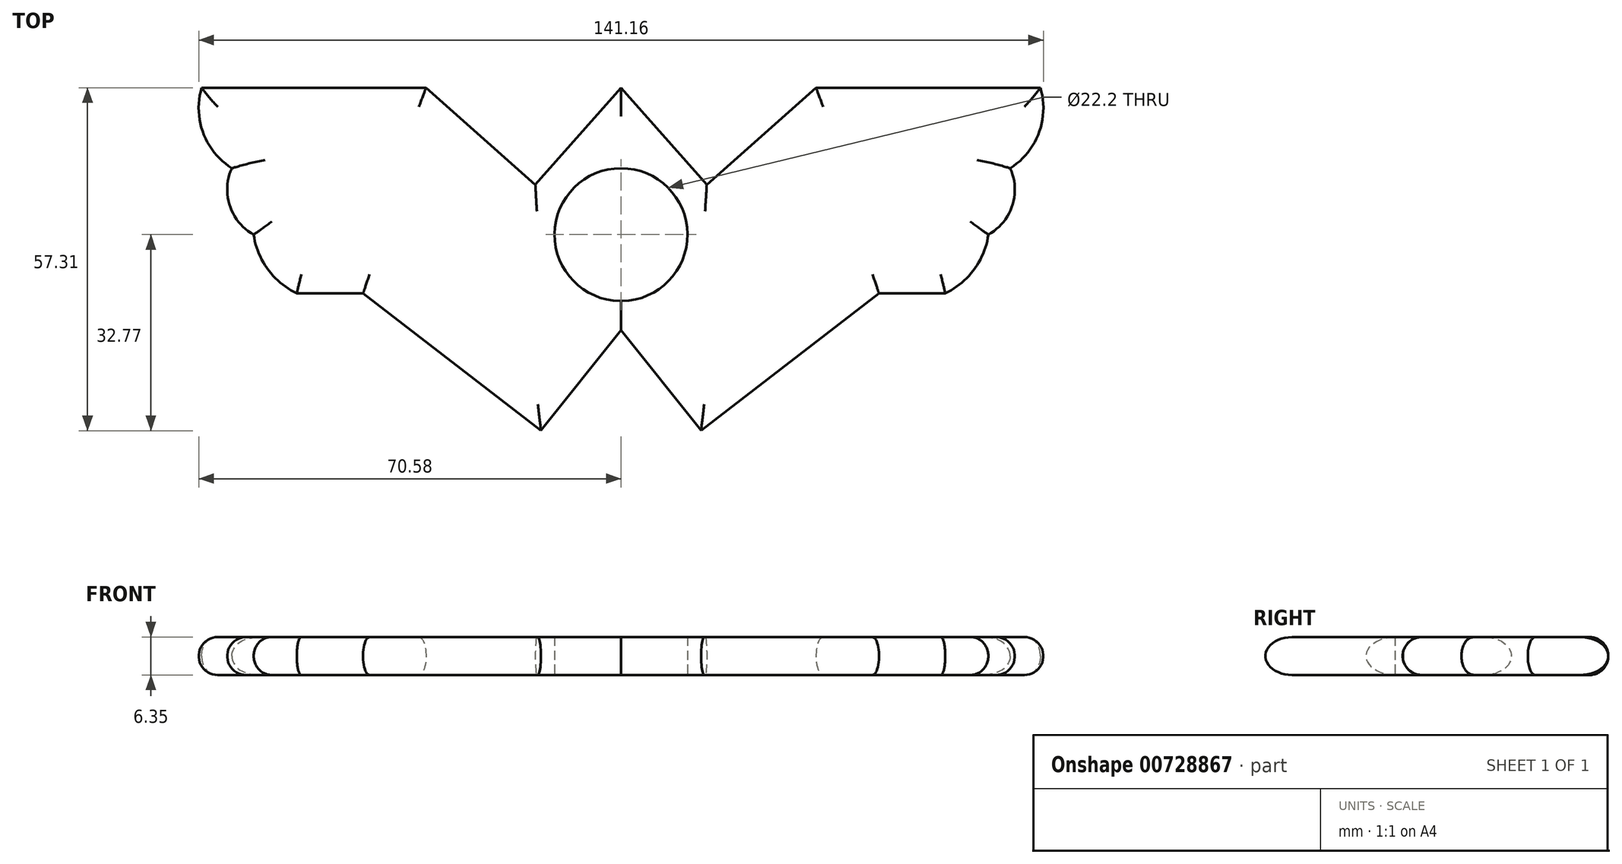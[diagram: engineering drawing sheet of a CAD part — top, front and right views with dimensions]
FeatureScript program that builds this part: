
annotation { "Feature Type Name" : "Feature", "Feature Type Description" : "" }
export const myFeature = defineFeature(function(context is Context, id is Id, definition is map)
    precondition{}
    {
        {
            var Q0;
            Q0=qCreatedBy(makeId("Top.planeOp"),FACE);
            var sketch = newSketch(context, id + "F0", { "sketchPlane" : qUnion([Q0])});
            skLineSegment(sketch, "E0", {"start": v(0, 24.54) * mm, "end": v(-14.33, 8.37) * mm});
            skLineSegment(sketch, "E1", {"start": v(-14.33, 8.37) * mm, "end": v(-32.58, 24.54) * mm});
            skLineSegment(sketch, "E2", {"start": v(-32.58, 24.54) * mm, "end": v(-56.32, 24.54) * mm});
            skLineSegment(sketch, "E3.MirrorCS", {"start": v(0, 24.54) * mm, "end": v(14.33, 8.37) * mm});
            skLineSegment(sketch, "E4.MirrorCS", {"start": v(32.58, 24.54) * mm, "end": v(56.32, 24.54) * mm});
            skLineSegment(sketch, "E5.MirrorCS", {"start": v(14.33, 8.37) * mm, "end": v(32.58, 24.54) * mm});
            skLineSegment(sketch, "E6.1.0.1", {"start": v(-14.14, -13.63) * mm, "end": v(-18.37, -9.88) * mm});
            skLineSegment(sketch, "E6.1.0.3", {"start": v(8.6, -6.95) * mm, "end": v(14.51, -13.63) * mm});
            skLineSegment(sketch, "E6.1.0.4", {"start": v(14.51, -13.63) * mm, "end": v(18.55, -10.06) * mm});
            skPoint(sketch, "E7.orphan", {"position": v(32.77, 2.54) * mm});
            skLineSegment(sketch, "E8", {"start": v(39.4, 8.41) * mm, "end": v(42.4, 11.07) * mm});
            skLineSegment(sketch, "E9", {"start": v(42.4, 11.07) * mm, "end": v(51.59, 11.08) * mm});
            skLineSegment(sketch, "E10", {"start": v(42.21, 0) * mm, "end": v(51.59, 0) * mm});
            skLineSegment(sketch, "E11", {"start": v(51.59, 11.08) * mm, "end": v(51.59, 11.08) * mm});
            skLineSegment(sketch, "E12", {"start": v(56.32, 24.54) * mm, "end": v(70.09, 24.54) * mm});
            skLineSegment(sketch, "E13", {"start": v(51.59, 11.08) * mm, "end": v(65.04, 11.1) * mm});
            skArc(sketch, "E14", {"start": v(65.04, 11.1) * mm, "mid": v(69.82, 16.97) * mm, "end": v(70.09, 24.54) * mm});
            skArc(sketch, "E15", {"start": v(61.4, 0) * mm, "mid": v(65.39, 4.84) * mm, "end": v(65.04, 11.1) * mm});
            skLineSegment(sketch, "E16.MirrorCS", {"start": v(-39.4, 8.41) * mm, "end": v(-42.4, 11.07) * mm});
            skLineSegment(sketch, "E17.MirrorCS", {"start": v(-42.4, 11.07) * mm, "end": v(-51.59, 11.08) * mm});
            skLineSegment(sketch, "E18.MirrorCS", {"start": v(-51.59, 11.08) * mm, "end": v(-51.59, 11.08) * mm});
            skLineSegment(sketch, "E19.MirrorCS", {"start": v(-51.59, 11.08) * mm, "end": v(-65.04, 11.1) * mm});
            skLineSegment(sketch, "E20.MirrorCS", {"start": v(-56.32, 24.54) * mm, "end": v(-70.09, 24.54) * mm});
            skArc(sketch, "E21.MirrorCS", {"start": v(-65.04, 11.1) * mm, "mid": v(-69.82, 16.97) * mm, "end": v(-70.09, 24.54) * mm});
            skArc(sketch, "E22.MirrorCS", {"start": v(-61.4, 0) * mm, "mid": v(-65.39, 4.84) * mm, "end": v(-65.04, 11.1) * mm});
            skLineSegment(sketch, "E23.1.0.0", {"start": v(0, -15.96) * mm, "end": v(-13.37, -32.77) * mm});
            skLineSegment(sketch, "E23.1.0.3", {"start": v(-43.11, -9.81) * mm, "end": v(-54.19, -9.81) * mm});
            skLineSegment(sketch, "E23.1.0.4", {"start": v(-52.8, -9.4) * mm, "end": v(-54.19, -9.81) * mm});
            skLineSegment(sketch, "E24", {"start": v(51.59, 0) * mm, "end": v(61.4, 0) * mm});
            skLineSegment(sketch, "E25.MirrorCS", {"start": v(-51.59, 0) * mm, "end": v(-61.4, 0) * mm});
            skLineSegment(sketch, "E26.MirrorCS", {"start": v(-42.21, 0) * mm, "end": v(-51.59, 0) * mm});
            skArc(sketch, "E27.MirrorCS", {"start": v(-54.19, -9.81) * mm, "mid": v(-59.02, -5.8) * mm, "end": v(-61.4, 0) * mm});
            skPoint(sketch, "E28.orphan", {"position": v(58.34, -6.26) * mm});
            skPoint(sketch, "E29.orphan", {"position": v(-65.12, -13.12) * mm});
            skLineSegment(sketch, "E30.trimOffspring", {"start": v(-8.41, -7.16) * mm, "end": v(-14.14, -13.63) * mm});
            skPoint(sketch, "E31.orphan", {"position": v(0.19, 2.54) * mm});
            skPoint(sketch, "E32.orphan", {"position": v(-32.77, 2.54) * mm});
            skPoint(sketch, "E33.orphan", {"position": v(-32.4, 2.54) * mm});
            skLineSegment(sketch, "E34.trimOffspring", {"start": v(-56.16, 0) * mm, "end": v(-56.13, 2.54) * mm, "construction": true});
            skLineSegment(sketch, "E35", {"start": v(-61.4, 0) * mm, "end": v(-42.21, 0) * mm});
            skLineSegment(sketch, "E36", {"start": v(42.21, 0) * mm, "end": v(61.4, 0) * mm});
            skPoint(sketch, "E23.1.0.7.end.orphan", {"position": v(59.36, -13.37) * mm});
            skPoint(sketch, "E23.1.0.8.start.orphan", {"position": v(50.04, -13.37) * mm});
            skPoint(sketch, "E37.start.orphan", {"position": v(54.19, -9.81) * mm});
            skLineSegment(sketch, "E38.MirrorCS", {"start": v(0, -15.96) * mm, "end": v(13.37, -32.77) * mm});
            skLineSegment(sketch, "E39.MirrorCS", {"start": v(43.11, -9.81) * mm, "end": v(54.19, -9.81) * mm});
            skArc(sketch, "E40.MirrorCS", {"start": v(54.19, -9.81) * mm, "mid": v(59.02, -5.8) * mm, "end": v(61.4, 0) * mm});
            skPoint(sketch, "E23.1.0.2.start.orphan", {"position": v(-27.1, -21.7) * mm});
            skPoint(sketch, "E23.1.0.1.end.orphan", {"position": v(-27.42, -21.7) * mm});
            skPoint(sketch, "E41.MirrorCS.end.orphan", {"position": v(27.42, -21.7) * mm});
            skPoint(sketch, "E41.MirrorCS.start.orphan", {"position": v(13.37, -32.77) * mm});
            skPoint(sketch, "E42.MirrorCS.end.orphan", {"position": v(43.11, -9.81) * mm});
            skPoint(sketch, "E42.MirrorCS.start.orphan", {"position": v(27.1, -21.7) * mm});
            skLineSegment(sketch, "E43", {"start": v(-43.11, -9.81) * mm, "end": v(-13.37, -32.77) * mm});
            skLineSegment(sketch, "E44.MirrorCS", {"start": v(43.11, -9.81) * mm, "end": v(13.37, -32.77) * mm});
            skCircle(sketch, "E45", {"center": v(0, 0) * mm, "radius": 11.1 * mm});
            skLineSegment(sketch, "E46", {"start": v(-39.4, 8.41) * mm, "end": v(-18.37, -9.88) * mm});
            skLineSegment(sketch, "E47", {"start": v(39.4, 8.41) * mm, "end": v(18.55, -10.06) * mm});
            skSolve(sketch);
        }
        {
            var Q0;
            Q0=qSketchRegion(id+"F0",true);
            extrude(context, id + "F1", {"entities" : qUnion([Q0]), "depth" : 6.35 * mm, "offsetDistance" : 25.4 * mm});
        }
        {
            var Q0;
            Q0=makeQuery(id+"F1.opExtrude","CAP_EDGE",EDGE,{"disambiguationData":[OSD([sQuery(id+"F0.wireOp",EDGE,"E2"),sQuery(id+"F0.wireOp",EDGE,"E20.MirrorCS")])],"isStart":false});
            var Q1;
            Q1=makeQuery(id+"F1.opExtrude","CAP_EDGE",EDGE,{"disambiguationData":[OSD([sQuery(id+"F0.wireOp",EDGE,"E22.MirrorCS")])],"isStart":false});
            var Q2;
            Q2=makeQuery(id+"F1.opExtrude","CAP_EDGE",EDGE,{"disambiguationData":[OSD([sQuery(id+"F0.wireOp",EDGE,"E27.MirrorCS")])],"isStart":false});
            var Q3;
            Q3=makeQuery(id+"F1.opExtrude","CAP_EDGE",EDGE,{"disambiguationData":[OSD([sQuery(id+"F0.wireOp",EDGE,"E23.1.0.3")])],"isStart":false});
            var Q4;
            Q4=makeQuery(id+"F1.opExtrude","CAP_EDGE",EDGE,{"disambiguationData":[OSD([sQuery(id+"F0.wireOp",EDGE,"E43")])],"isStart":false});
            var Q5;
            Q5=makeQuery(id+"F1.opExtrude","CAP_EDGE",EDGE,{"disambiguationData":[OSD([sQuery(id+"F0.wireOp",EDGE,"E23.1.0.0")])],"isStart":false});
            var Q6;
            Q6=makeQuery(id+"F1.opExtrude","CAP_EDGE",EDGE,{"disambiguationData":[OSD([sQuery(id+"F0.wireOp",EDGE,"E38.MirrorCS")])],"isStart":false});
            var Q7;
            Q7=makeQuery(id+"F1.opExtrude","CAP_EDGE",EDGE,{"disambiguationData":[OSD([sQuery(id+"F0.wireOp",EDGE,"E44.MirrorCS")])],"isStart":false});
            var Q8;
            Q8=makeQuery(id+"F1.opExtrude","CAP_EDGE",EDGE,{"disambiguationData":[OSD([sQuery(id+"F0.wireOp",EDGE,"E39.MirrorCS")])],"isStart":false});
            var Q9;
            Q9=makeQuery(id+"F1.opExtrude","CAP_EDGE",EDGE,{"disambiguationData":[OSD([sQuery(id+"F0.wireOp",EDGE,"E40.MirrorCS")])],"isStart":false});
            var Q10;
            Q10=makeQuery(id+"F1.opExtrude","CAP_EDGE",EDGE,{"disambiguationData":[OSD([sQuery(id+"F0.wireOp",EDGE,"E1")])],"isStart":false});
            var Q11;
            Q11=makeQuery(id+"F1.opExtrude","CAP_EDGE",EDGE,{"disambiguationData":[OSD([sQuery(id+"F0.wireOp",EDGE,"E0")])],"isStart":false});
            var Q12;
            Q12=makeQuery(id+"F1.opExtrude","CAP_EDGE",EDGE,{"disambiguationData":[OSD([sQuery(id+"F0.wireOp",EDGE,"E3.MirrorCS")])],"isStart":false});
            var Q13;
            Q13=makeQuery(id+"F1.opExtrude","CAP_EDGE",EDGE,{"disambiguationData":[OSD([sQuery(id+"F0.wireOp",EDGE,"E5.MirrorCS")])],"isStart":false});
            var Q14;
            Q14=makeQuery(id+"F1.opExtrude","CAP_EDGE",EDGE,{"disambiguationData":[OSD([sQuery(id+"F0.wireOp",EDGE,"E4.MirrorCS"),sQuery(id+"F0.wireOp",EDGE,"E12")])],"isStart":false});
            var Q15;
            Q15=makeQuery(id+"F1.opExtrude","CAP_EDGE",EDGE,{"disambiguationData":[OSD([sQuery(id+"F0.wireOp",EDGE,"E14")])],"isStart":false});
            var Q16;
            Q16=makeQuery(id+"F1.opExtrude","CAP_EDGE",EDGE,{"disambiguationData":[OSD([sQuery(id+"F0.wireOp",EDGE,"E4.MirrorCS"),sQuery(id+"F0.wireOp",EDGE,"E12")])],"isStart":true});
            var Q17;
            Q17=makeQuery(id+"F1.opExtrude","CAP_EDGE",EDGE,{"disambiguationData":[OSD([sQuery(id+"F0.wireOp",EDGE,"E5.MirrorCS")])],"isStart":true});
            var Q18;
            Q18=makeQuery(id+"F1.opExtrude","CAP_EDGE",EDGE,{"disambiguationData":[OSD([sQuery(id+"F0.wireOp",EDGE,"E21.MirrorCS")])],"isStart":true});
            var Q19;
            Q19=makeQuery(id+"F1.opExtrude","CAP_EDGE",EDGE,{"disambiguationData":[OSD([sQuery(id+"F0.wireOp",EDGE,"E27.MirrorCS")])],"isStart":true});
            var Q20;
            Q20=makeQuery(id+"F1.opExtrude","CAP_EDGE",EDGE,{"disambiguationData":[OSD([sQuery(id+"F0.wireOp",EDGE,"E23.1.0.3")])],"isStart":true});
            var Q21;
            Q21=makeQuery(id+"F1.opExtrude","CAP_EDGE",EDGE,{"disambiguationData":[OSD([sQuery(id+"F0.wireOp",EDGE,"E43")])],"isStart":true});
            var Q22;
            Q22=makeQuery(id+"F1.opExtrude","CAP_EDGE",EDGE,{"disambiguationData":[OSD([sQuery(id+"F0.wireOp",EDGE,"E23.1.0.0")])],"isStart":true});
            var Q23;
            Q23=makeQuery(id+"F1.opExtrude","CAP_EDGE",EDGE,{"disambiguationData":[OSD([sQuery(id+"F0.wireOp",EDGE,"E38.MirrorCS")])],"isStart":true});
            var Q24;
            Q24=makeQuery(id+"F1.opExtrude","CAP_EDGE",EDGE,{"disambiguationData":[OSD([sQuery(id+"F0.wireOp",EDGE,"E14")])],"isStart":true});
            var Q25;
            Q25=makeQuery(id+"F1.opExtrude","CAP_EDGE",EDGE,{"disambiguationData":[OSD([sQuery(id+"F0.wireOp",EDGE,"E44.MirrorCS")])],"isStart":true});
            var Q26;
            Q26=makeQuery(id+"F1.opExtrude","CAP_EDGE",EDGE,{"disambiguationData":[OSD([sQuery(id+"F0.wireOp",EDGE,"E39.MirrorCS")])],"isStart":true});
            var Q27;
            Q27=makeQuery(id+"F1.opExtrude","CAP_EDGE",EDGE,{"disambiguationData":[OSD([sQuery(id+"F0.wireOp",EDGE,"E40.MirrorCS")])],"isStart":true});
            var Q28;
            Q28=makeQuery(id+"F1.opExtrude","CAP_EDGE",EDGE,{"disambiguationData":[OSD([sQuery(id+"F0.wireOp",EDGE,"E15")])],"isStart":false});
            var Q29;
            Q29=makeQuery(id+"F1.opExtrude","CAP_EDGE",EDGE,{"disambiguationData":[OSD([sQuery(id+"F0.wireOp",EDGE,"E15")])],"isStart":true});
            var Q30;
            Q30=makeQuery(id+"F1.opExtrude","CAP_EDGE",EDGE,{"disambiguationData":[OSD([sQuery(id+"F0.wireOp",EDGE,"E0")])],"isStart":true});
            var Q31;
            Q31=makeQuery(id+"F1.opExtrude","CAP_EDGE",EDGE,{"disambiguationData":[OSD([sQuery(id+"F0.wireOp",EDGE,"E3.MirrorCS")])],"isStart":true});
            var Q32;
            Q32=makeQuery(id+"F1.opExtrude","CAP_EDGE",EDGE,{"disambiguationData":[OSD([sQuery(id+"F0.wireOp",EDGE,"E1")])],"isStart":true});
            var Q33;
            Q33=makeQuery(id+"F1.opExtrude","CAP_EDGE",EDGE,{"disambiguationData":[OSD([sQuery(id+"F0.wireOp",EDGE,"E2"),sQuery(id+"F0.wireOp",EDGE,"E20.MirrorCS")])],"isStart":true});
            var Q34;
            Q34=makeQuery(id+"F1.opExtrude","CAP_EDGE",EDGE,{"disambiguationData":[OSD([sQuery(id+"F0.wireOp",EDGE,"E22.MirrorCS")])],"isStart":true});
            var Q35;
            Q35=makeQuery(id+"F1.opExtrude","CAP_EDGE",EDGE,{"disambiguationData":[OSD([sQuery(id+"F0.wireOp",EDGE,"E21.MirrorCS")])],"isStart":false});
            fillet(context, id + "F2", {"entities" : qUnion([Q0, Q1, Q2, Q3, Q4, Q5, Q6, Q7, Q8, Q9, Q10, Q11, Q12, Q13, Q14, Q15, Q16, Q17, Q18, Q19, Q20, Q21, Q22, Q23, Q24, Q25, Q26, Q27, Q28, Q29, Q30, Q31, Q32, Q33, Q34, Q35]), "radius" : 3.17 * mm, "tangentPropagation" : true, "allowEdgeOverflow" : false});
        }
    });
